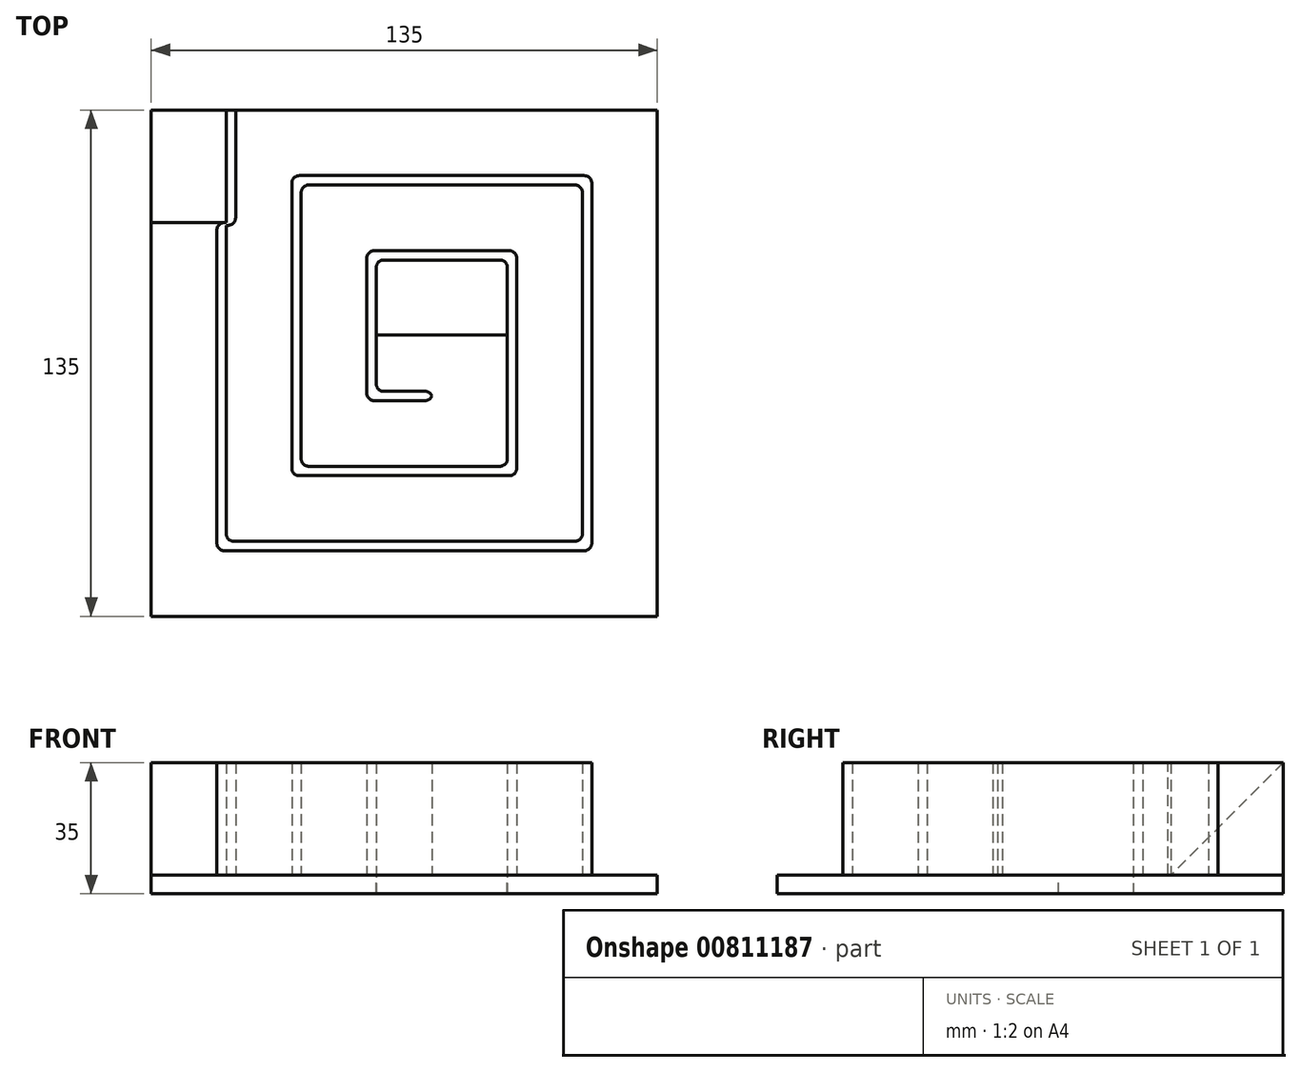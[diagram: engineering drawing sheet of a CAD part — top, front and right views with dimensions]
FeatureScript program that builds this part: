
annotation { "Feature Type Name" : "Feature", "Feature Type Description" : "" }
export const myFeature = defineFeature(function(context is Context, id is Id, definition is map)
    precondition{}
    {
        {
            var Q0;
            Q0=qCreatedBy(makeId("Top.planeOp"),FACE);
            var sketch = newSketch(context, id + "F0", { "sketchPlane" : qUnion([Q0])});
            skLineSegment(sketch, "E0.bottom", {"start": v(-67.5, 67.5) * mm, "end": v(67.5, 67.5) * mm});
            skLineSegment(sketch, "E0.top", {"start": v(-67.5, -67.5) * mm, "end": v(67.5, -67.5) * mm});
            skLineSegment(sketch, "E0.left", {"start": v(-67.5, 67.5) * mm, "end": v(-67.5, -67.5) * mm});
            skLineSegment(sketch, "E0.right", {"start": v(67.5, 67.5) * mm, "end": v(67.5, -67.5) * mm});
            skPoint(sketch, "E0.middle", {"position": v(0, 0) * mm});
            skLineSegment(sketch, "E1", {"start": v(-47.5, 67.5) * mm, "end": v(-47.5, 37.5) * mm});
            skLineSegment(sketch, "E2", {"start": v(-47.5, 37.5) * mm, "end": v(-67.5, 37.5) * mm});
            skSolve(sketch);
        }
        {
            var Q0;
            {var subQ2=sQuery(id+"F0.wireOp",EDGE,"E0.top");Q0=makeQuery(id+"F0.imprint","IMPRINT",FACE,{"disambiguationData":[TD([[makeQuery(id+"F0.imprint","IMPRINT",EDGE,{"derivedFrom":subQ2}),1.0]])]});}
            extrude(context, id + "F1", {"entities" : qUnion([Q0]), "depth" : 5 * mm, "offsetDistance" : 25 * mm});
        }
        {
            var Q0;
            {var subQ3=sQuery(id+"F0.wireOp",EDGE,"E1");Q0=makeQuery(id+"F0.imprint","IMPRINT",FACE,{"disambiguationData":[TD([[makeQuery(id+"F0.imprint","IMPRINT",EDGE,{"derivedFrom":subQ3}),-1.0]])]});}
            extrude(context, id + "F2", {"entities" : qUnion([Q0]), "operationType" : NewBodyOperationType.ADD, "depth" : 35 * mm, "offsetDistance" : 25 * mm});
        }
        {
            var Q0;
            Q0=makeQuery(id+"F2.opExtrude","SWEPT_FACE",FACE,{"disambiguationData":[OSD([sQuery(id+"F0.wireOp",EDGE,"E1")])]});
            var sketch = newSketch(context, id + "F3", { "sketchPlane" : qUnion([Q0])});
            skLineSegment(sketch, "E3", {"start": v(67.5, 35) * mm, "end": v(37.5, 5) * mm});
            skSolve(sketch);
        }
        {
            var Q0;
            Q0=makeQuery(id+"F3.imprint","IMPRINT",FACE,{"disambiguationData":[TD([[makeQuery(id+"F3.imprint","IMPRINT",EDGE,{"derivedFrom":sQuery(id+"F3.wireOp",EDGE,"E3")}),-1.0]])]});
            extrude(context, id + "F4", {"entities" : qUnion([Q0]), "operationType" : NewBodyOperationType.REMOVE, "oppositeDirection" : true, "depth" : 20 * mm, "offsetDistance" : 25 * mm});
        }
        {
            var Q0;
            Q0=makeQuery(id+"F1.opExtrude","CAP_FACE",FACE,{"disambiguationData":[OSD([sQuery(id+"F0.wireOp",EDGE,"E0.bottom"),sQuery(id+"F0.wireOp",EDGE,"E0.top"),sQuery(id+"F0.wireOp",EDGE,"E0.left"),sQuery(id+"F0.wireOp",EDGE,"E0.right"),sQuery(id+"F0.wireOp",EDGE,"E1"),sQuery(id+"F0.wireOp",EDGE,"E2")])],"isStart":false});
            var sketch = newSketch(context, id + "F5", { "sketchPlane" : qUnion([Q0])});
            skLineSegment(sketch, "E4", {"start": v(-47.5, 37.5) * mm, "end": v(-47.5, -47.5) * mm});
            skLineSegment(sketch, "E5", {"start": v(-47.5, -47.5) * mm, "end": v(47.5, -47.5) * mm});
            skLineSegment(sketch, "E6", {"start": v(47.5, -47.5) * mm, "end": v(47.5, 47.5) * mm});
            skLineSegment(sketch, "E7", {"start": v(47.5, 47.5) * mm, "end": v(-27.5, 47.5) * mm});
            skLineSegment(sketch, "E8", {"start": v(-27.5, 47.5) * mm, "end": v(-27.5, -27.5) * mm});
            skLineSegment(sketch, "E9", {"start": v(-27.5, -27.5) * mm, "end": v(27.5, -27.5) * mm});
            skLineSegment(sketch, "E10", {"start": v(27.5, -27.5) * mm, "end": v(27.5, 27.5) * mm});
            skLineSegment(sketch, "E11", {"start": v(27.5, 27.5) * mm, "end": v(-7.5, 27.5) * mm});
            skLineSegment(sketch, "E12", {"start": v(-7.5, 27.5) * mm, "end": v(-7.5, -7.5) * mm});
            skLineSegment(sketch, "E13", {"start": v(-7.5, -7.5) * mm, "end": v(7.5, -7.5) * mm});
            skLineSegment(sketch, "E14.0", {"start": v(50, -50) * mm, "end": v(50, 50) * mm});
            skLineSegment(sketch, "E14.1", {"start": v(-50, -50) * mm, "end": v(50, -50) * mm});
            skLineSegment(sketch, "E14.2", {"start": v(-50, 37.5) * mm, "end": v(-50, -50) * mm});
            skLineSegment(sketch, "E15.0", {"start": v(30, -30) * mm, "end": v(30, 30) * mm});
            skLineSegment(sketch, "E15.1", {"start": v(-30, -30) * mm, "end": v(30, -30) * mm});
            skLineSegment(sketch, "E15.2", {"start": v(-30, 50) * mm, "end": v(-30, -30) * mm});
            skLineSegment(sketch, "E15.3", {"start": v(50, 50) * mm, "end": v(-30, 50) * mm});
            skLineSegment(sketch, "E16.0", {"start": v(-10, -10) * mm, "end": v(7.5, -10) * mm});
            skLineSegment(sketch, "E16.1", {"start": v(-10, 30) * mm, "end": v(-10, -10) * mm});
            skLineSegment(sketch, "E16.2", {"start": v(30, 30) * mm, "end": v(-10, 30) * mm});
            skLineSegment(sketch, "E17", {"start": v(7.5, -7.5) * mm, "end": v(7.5, -10) * mm});
            skSolve(sketch);
        }
        {
            var Q0;
            {var subQ0=sQuery(id+"F5.wireOp",EDGE,"E4");Q0=makeQuery(id+"F5.imprint","IMPRINT",FACE,{"disambiguationData":[TD([[makeQuery(id+"F5.imprint","IMPRINT",EDGE,{"derivedFrom":subQ0}),-1.0]])]});}
            extrude(context, id + "F6", {"entities" : qUnion([Q0]), "operationType" : NewBodyOperationType.ADD, "depth" : 30 * mm, "offsetDistance" : 25 * mm});
        }
        {
            var Q0;
            Q0=makeQuery(id+"F2.opExtrude","SWEPT_FACE",FACE,{"disambiguationData":[OSD([sQuery(id+"F0.wireOp",EDGE,"E1")])]});
            var sketch = newSketch(context, id + "F7", { "sketchPlane" : qUnion([Q0])});
            skLineSegment(sketch, "E18.bottom", {"start": v(67.5, 5) * mm, "end": v(36.76, 5) * mm});
            skLineSegment(sketch, "E18.top", {"start": v(67.5, 35) * mm, "end": v(36.76, 35) * mm});
            skLineSegment(sketch, "E18.left", {"start": v(67.5, 5) * mm, "end": v(67.5, 35) * mm});
            skLineSegment(sketch, "E18.right", {"start": v(36.76, 5) * mm, "end": v(36.76, 35) * mm});
            skSolve(sketch);
        }
        {
            var Q0;
            Q0=makeQuery(id+"F7.imprint","IMPRINT",FACE,{"disambiguationData":[TD([[makeQuery(id+"F7.imprint","IMPRINT",EDGE,{"derivedFrom":sQuery(id+"F7.wireOp",EDGE,"E18.top")}),1.0]])]});
            var Q1;
            {var subQ0=sQuery(id+"F7.wireOp",EDGE,"E18.left");Q1=makeQuery(id+"F7.imprint","IMPRINT",FACE,{"disambiguationData":[TD([[makeQuery(id+"F7.imprint","IMPRINT",EDGE,{"derivedFrom":subQ0}),-1.0]])]});}
            extrude(context, id + "F8", {"entities" : qUnion([Q0, Q1]), "operationType" : NewBodyOperationType.ADD, "depth" : 2.5 * mm, "offsetDistance" : 25 * mm});
        }
        {
            var Q0;
            Q0=makeQuery(id+"F1.opExtrude","CAP_FACE",FACE,{"disambiguationData":[OSD([sQuery(id+"F0.wireOp",EDGE,"E0.bottom"),sQuery(id+"F0.wireOp",EDGE,"E0.top"),sQuery(id+"F0.wireOp",EDGE,"E0.left"),sQuery(id+"F0.wireOp",EDGE,"E0.right"),sQuery(id+"F0.wireOp",EDGE,"E1"),sQuery(id+"F0.wireOp",EDGE,"E2")])],"isStart":false});
            var sketch = newSketch(context, id + "F9", { "sketchPlane" : qUnion([Q0])});
            skLineSegment(sketch, "E19.bottom", {"start": v(-7.5, 27.5) * mm, "end": v(27.5, 27.5) * mm});
            skLineSegment(sketch, "E19.top", {"start": v(-7.5, 7.5) * mm, "end": v(27.5, 7.5) * mm});
            skLineSegment(sketch, "E19.left", {"start": v(-7.5, 27.5) * mm, "end": v(-7.5, 7.5) * mm});
            skLineSegment(sketch, "E19.right", {"start": v(27.5, 27.5) * mm, "end": v(27.5, 7.5) * mm});
            skSolve(sketch);
        }
        {
            var Q0;
            Q0 = qSketchRegion(id + "F9", true);
            extrude(context, id + "F10", {"entities" : qUnion([Q0]), "operationType" : NewBodyOperationType.REMOVE, "oppositeDirection" : true, "depth" : 5 * mm, "offsetDistance" : 25 * mm});
        }
        {
            var Q0;
            Q0=makeQuery(id+"F6.opExtrude","SWEPT_EDGE",EDGE,{"disambiguationData":[OSD([sQuery(id+"F5.wireOp",EDGE,"E14.0"),sQuery(id+"F5.wireOp",EDGE,"E14.1")])]});
            var Q1;
            Q1=makeQuery(id+"F6.opExtrude","SWEPT_EDGE",EDGE,{"disambiguationData":[OSD([sQuery(id+"F5.wireOp",EDGE,"E14.1"),sQuery(id+"F5.wireOp",EDGE,"E14.2")])]});
            var Q2;
            Q2=makeQuery(id+"F6.opExtrude","SWEPT_EDGE",EDGE,{"disambiguationData":[OSD([sQuery(id+"F5.wireOp",EDGE,"E14.0"),sQuery(id+"F5.wireOp",EDGE,"E15.3")])]});
            var Q3;
            Q3=makeQuery(id+"F8.opExtrude","CAP_EDGE",EDGE,{"disambiguationData":[OSD([sQuery(id+"F7.wireOp",EDGE,"E18.right")])],"isStart":false});
            var Q4;
            Q4=makeQuery(id+"F6.opExtrude","SWEPT_EDGE",EDGE,{"disambiguationData":[OSD([sQuery(id+"F0.wireOp",EDGE,"E1"),sQuery(id+"F0.wireOp",EDGE,"E2"),sQuery(id+"F3.wireOp",EDGE,"E3"),sQuery(id+"F5.wireOp",EDGE,"E14.2")])]});
            var Q5;
            Q5=makeQuery(id+"F6.opExtrude","SWEPT_EDGE",EDGE,{"disambiguationData":[OSD([sQuery(id+"F5.wireOp",EDGE,"E15.2"),sQuery(id+"F5.wireOp",EDGE,"E15.3")])]});
            var Q6;
            Q6=makeQuery(id+"F6.opExtrude","SWEPT_EDGE",EDGE,{"disambiguationData":[OSD([sQuery(id+"F5.wireOp",EDGE,"E15.0"),sQuery(id+"F5.wireOp",EDGE,"E16.2")])]});
            var Q7;
            Q7=makeQuery(id+"F6.opExtrude","SWEPT_EDGE",EDGE,{"disambiguationData":[OSD([sQuery(id+"F5.wireOp",EDGE,"E13"),sQuery(id+"F5.wireOp",EDGE,"E17")])]});
            var Q8;
            Q8=makeQuery(id+"F6.opExtrude","SWEPT_EDGE",EDGE,{"disambiguationData":[OSD([sQuery(id+"F5.wireOp",EDGE,"E16.1"),sQuery(id+"F5.wireOp",EDGE,"E16.2")])]});
            var Q9;
            Q9=makeQuery(id+"F6.opExtrude","SWEPT_EDGE",EDGE,{"disambiguationData":[OSD([sQuery(id+"F5.wireOp",EDGE,"E15.0"),sQuery(id+"F5.wireOp",EDGE,"E15.1")])]});
            var Q10;
            Q10=makeQuery(id+"F6.opExtrude","SWEPT_EDGE",EDGE,{"disambiguationData":[OSD([sQuery(id+"F5.wireOp",EDGE,"E15.1"),sQuery(id+"F5.wireOp",EDGE,"E15.2")])]});
            var Q11;
            Q11=makeQuery(id+"F6.opExtrude","SWEPT_EDGE",EDGE,{"disambiguationData":[OSD([sQuery(id+"F5.wireOp",EDGE,"E16.0"),sQuery(id+"F5.wireOp",EDGE,"E16.1")])]});
            var Q12;
            Q12=makeQuery(id+"F6.opExtrude","SWEPT_EDGE",EDGE,{"disambiguationData":[OSD([sQuery(id+"F5.wireOp",EDGE,"E16.0"),sQuery(id+"F5.wireOp",EDGE,"E17")])]});
            fillet(context, id + "F11", {"entities" : qUnion([Q0, Q1, Q2, Q3, Q4, Q5, Q6, Q7, Q8, Q9, Q10, Q11, Q12]), "radius" : 2 * mm, "tangentPropagation" : true, "allowEdgeOverflow" : false});
        }
        {
            var Q0;
            Q0=makeQuery(id+"F6.opExtrude","SWEPT_EDGE",EDGE,{"disambiguationData":[OSD([sQuery(id+"F5.wireOp",EDGE,"E6"),sQuery(id+"F5.wireOp",EDGE,"E7")])]});
            var Q1;
            Q1=makeQuery(id+"F10.boolean.opBoolean","MERGE",EDGE,{"derivedFrom":[makeQuery(id+"F6.opExtrude","SWEPT_EDGE",EDGE,{"disambiguationData":[OSD([sQuery(id+"F5.wireOp",EDGE,"E10"),sQuery(id+"F5.wireOp",EDGE,"E11")])]}),makeQuery(id+"F10.opExtrude","SWEPT_EDGE",EDGE,{"disambiguationData":[OSD([sQuery(id+"F9.wireOp",EDGE,"E19.bottom"),sQuery(id+"F9.wireOp",EDGE,"E19.right")])]})]});
            var Q2;
            Q2=makeQuery(id+"F6.opExtrude","SWEPT_EDGE",EDGE,{"disambiguationData":[OSD([sQuery(id+"F5.wireOp",EDGE,"E5"),sQuery(id+"F5.wireOp",EDGE,"E6")])]});
            var Q3;
            Q3=makeQuery(id+"F6.opExtrude","SWEPT_EDGE",EDGE,{"disambiguationData":[OSD([sQuery(id+"F5.wireOp",EDGE,"E9"),sQuery(id+"F5.wireOp",EDGE,"E10")])]});
            var Q4;
            Q4=makeQuery(id+"F6.opExtrude","SWEPT_EDGE",EDGE,{"disambiguationData":[OSD([sQuery(id+"F5.wireOp",EDGE,"E4"),sQuery(id+"F5.wireOp",EDGE,"E5")])]});
            var Q5;
            Q5=makeQuery(id+"F6.opExtrude","SWEPT_EDGE",EDGE,{"disambiguationData":[OSD([sQuery(id+"F5.wireOp",EDGE,"E8"),sQuery(id+"F5.wireOp",EDGE,"E9")])]});
            var Q6;
            Q6=makeQuery(id+"F6.opExtrude","SWEPT_EDGE",EDGE,{"disambiguationData":[OSD([sQuery(id+"F5.wireOp",EDGE,"E12"),sQuery(id+"F5.wireOp",EDGE,"E13")])]});
            var Q7;
            Q7=makeQuery(id+"F8.opExtrude","CAP_EDGE",EDGE,{"disambiguationData":[OSD([sQuery(id+"F7.wireOp",EDGE,"E18.right")])],"isStart":true});
            var Q8;
            Q8=makeQuery(id+"F6.opExtrude","SWEPT_EDGE",EDGE,{"disambiguationData":[OSD([sQuery(id+"F5.wireOp",EDGE,"E7"),sQuery(id+"F5.wireOp",EDGE,"E8")])]});
            var Q9;
            Q9=makeQuery(id+"F10.boolean.opBoolean","MERGE",EDGE,{"derivedFrom":[makeQuery(id+"F6.opExtrude","SWEPT_EDGE",EDGE,{"disambiguationData":[OSD([sQuery(id+"F5.wireOp",EDGE,"E11"),sQuery(id+"F5.wireOp",EDGE,"E12")])]}),makeQuery(id+"F10.opExtrude","SWEPT_EDGE",EDGE,{"disambiguationData":[OSD([sQuery(id+"F9.wireOp",EDGE,"E19.bottom"),sQuery(id+"F9.wireOp",EDGE,"E19.left")])]})]});
            var Q10;
            Q10=makeQuery(id+"F6.opExtrude","SWEPT_EDGE",EDGE,{"disambiguationData":[OSD([sQuery(id+"F0.wireOp",EDGE,"E1"),sQuery(id+"F0.wireOp",EDGE,"E2"),sQuery(id+"F3.wireOp",EDGE,"E3"),sQuery(id+"F5.wireOp",EDGE,"E4")])]});
            fillet(context, id + "F12", {"entities" : qUnion([Q0, Q1, Q2, Q3, Q4, Q5, Q6, Q7, Q8, Q9, Q10]), "radius" : 2 * mm, "tangentPropagation" : true, "allowEdgeOverflow" : false});
        }
    });
